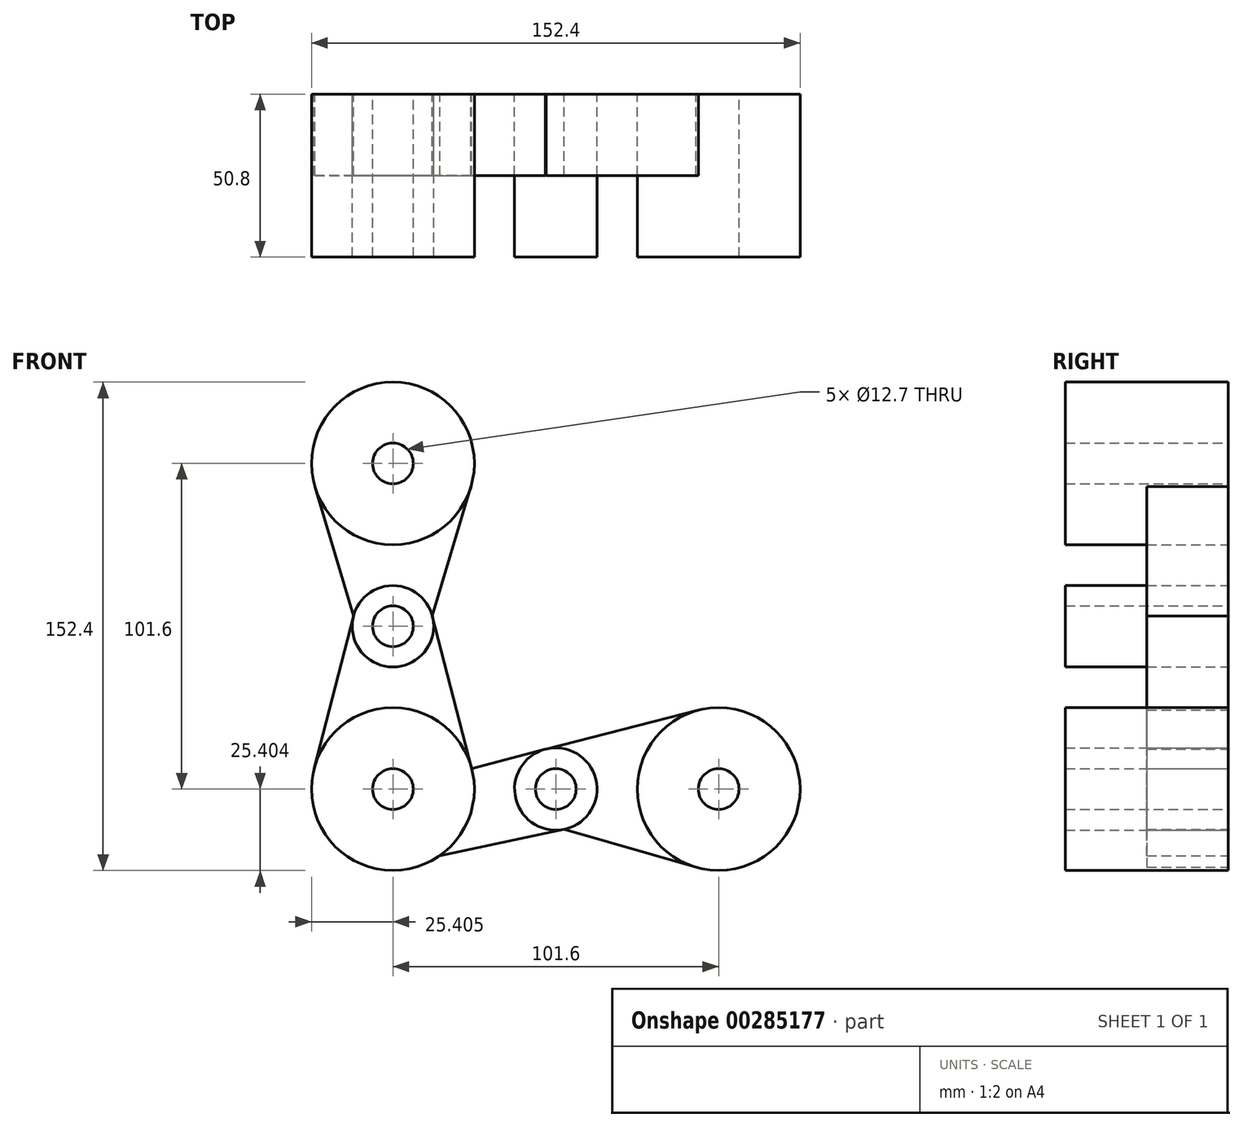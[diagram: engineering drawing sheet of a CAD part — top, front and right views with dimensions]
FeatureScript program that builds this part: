
annotation { "Feature Type Name" : "Feature", "Feature Type Description" : "" }
export const myFeature = defineFeature(function(context is Context, id is Id, definition is map)
    precondition{}
    {
        {
            var Q0;
            Q0=qCreatedBy(makeId("Front.planeOp"),FACE);
            var sketch = newSketch(context, id + "F0", { "sketchPlane" : qUnion([Q0])});
            skLineSegment(sketch, "E0", {"start": v(-81.49, -71.66) * mm, "end": v(-30.69, -71.66) * mm});
            skLineSegment(sketch, "E1", {"start": v(-30.69, -71.66) * mm, "end": v(20.11, -71.66) * mm});
            skLineSegment(sketch, "E2", {"start": v(-81.49, -71.66) * mm, "end": v(-81.49, -20.86) * mm});
            skLineSegment(sketch, "E3", {"start": v(-81.49, -20.86) * mm, "end": v(-81.49, 29.94) * mm});
            skCircle(sketch, "E4", {"center": v(20.11, -71.66) * mm, "radius": 25.4 * mm});
            skCircle(sketch, "E5", {"center": v(-81.49, -71.66) * mm, "radius": 25.4 * mm});
            skCircle(sketch, "E6", {"center": v(-81.49, 29.94) * mm, "radius": 25.4 * mm});
            skCircle(sketch, "E7", {"center": v(-81.49, -20.86) * mm, "radius": 12.7 * mm});
            skCircle(sketch, "E8", {"center": v(-30.69, -71.66) * mm, "radius": 12.85 * mm});
            skLineSegment(sketch, "E9", {"start": v(-57.15, 22.68) * mm, "end": v(-69.19, -17.68) * mm});
            skLineSegment(sketch, "E10", {"start": v(-69.19, -17.68) * mm, "end": v(-56.9, -65.3) * mm});
            skLineSegment(sketch, "E11", {"start": v(-56.9, -65.3) * mm, "end": v(-33.97, -59.24) * mm});
            skLineSegment(sketch, "E12", {"start": v(-33.97, -59.24) * mm, "end": v(13.84, -47.04) * mm});
            skLineSegment(sketch, "E13", {"start": v(-105.82, 22.68) * mm, "end": v(-93.78, -17.68) * mm});
            skLineSegment(sketch, "E14", {"start": v(-93.78, -17.68) * mm, "end": v(-106.08, -65.3) * mm});
            skLineSegment(sketch, "E15", {"start": v(-66.84, -92.4) * mm, "end": v(-28.03, -84.23) * mm});
            skLineSegment(sketch, "E16", {"start": v(-28.03, -84.23) * mm, "end": v(13.09, -96.06) * mm});
            skSolve(sketch);
        }
        {
            var Q0;
            {var subQ0=sQuery(id+"F0.wireOp",EDGE,"E6");var subQ1=makeQuery(id+"F0.imprint","INTERSECT",VERTEX,{"derivedFrom":[subQ0,sQuery(id+"F0.wireOp",EDGE,"E13")]});Q0=makeQuery(id+"F0.imprint","IMPRINT",FACE,{"disambiguationData":[TD([[makeQuery(id+"F0.imprint","IMPRINT",EDGE,{"disambiguationData":[TD([[subQ1,-1.0]])],"derivedFrom":subQ0}),1.0]])]});}
            var Q1;
            {var subQ3=sQuery(id+"F0.wireOp",EDGE,"E2");var subQ4=sQuery(id+"F0.wireOp",EDGE,"E0");var subQ5=makeQuery(id+"F0.imprint","INTERSECT",VERTEX,{"derivedFrom":[subQ4,subQ3]});Q1=makeQuery(id+"F0.imprint","IMPRINT",FACE,{"disambiguationData":[TD([[makeQuery(id+"F0.imprint","IMPRINT",EDGE,{"disambiguationData":[TD([[subQ5,-1.0]])],"derivedFrom":subQ4}),-1.0]])]});}
            var Q2;
            {var subQ0=sQuery(id+"F0.wireOp",EDGE,"E4");var subQ1=makeQuery(id+"F0.imprint","INTERSECT",VERTEX,{"derivedFrom":[subQ0,sQuery(id+"F0.wireOp",EDGE,"E12")]});Q2=makeQuery(id+"F0.imprint","IMPRINT",FACE,{"disambiguationData":[TD([[makeQuery(id+"F0.imprint","IMPRINT",EDGE,{"disambiguationData":[TD([[subQ1,-1.0]])],"derivedFrom":subQ0}),1.0]])]});}
            var Q3;
            {var subQ0=sQuery(id+"F0.wireOp",EDGE,"E3");var subQ1=sQuery(id+"F0.wireOp",EDGE,"E2");var subQ2=makeQuery(id+"F0.imprint","INTERSECT",VERTEX,{"derivedFrom":[subQ1,subQ0]});Q3=makeQuery(id+"F0.imprint","IMPRINT",FACE,{"disambiguationData":[TD([[makeQuery(id+"F0.imprint","IMPRINT",EDGE,{"disambiguationData":[TD([[subQ2,1.0]])],"derivedFrom":subQ1}),1.0]])]});}
            var Q4;
            {var subQ0=sQuery(id+"F0.wireOp",EDGE,"E3");var subQ1=sQuery(id+"F0.wireOp",EDGE,"E2");var subQ2=makeQuery(id+"F0.imprint","INTERSECT",VERTEX,{"derivedFrom":[subQ1,subQ0]});Q4=makeQuery(id+"F0.imprint","IMPRINT",FACE,{"disambiguationData":[TD([[makeQuery(id+"F0.imprint","IMPRINT",EDGE,{"disambiguationData":[TD([[subQ2,1.0]])],"derivedFrom":subQ1}),-1.0]])]});}
            var Q5;
            {var subQ0=sQuery(id+"F0.wireOp",EDGE,"E2");var subQ1=sQuery(id+"F0.wireOp",EDGE,"E0");var subQ2=makeQuery(id+"F0.imprint","INTERSECT",VERTEX,{"derivedFrom":[subQ1,subQ0]});Q5=makeQuery(id+"F0.imprint","IMPRINT",FACE,{"disambiguationData":[TD([[makeQuery(id+"F0.imprint","IMPRINT",EDGE,{"disambiguationData":[TD([[subQ2,-1.0]])],"derivedFrom":subQ1}),1.0]])]});}
            var Q6;
            {var subQ3=sQuery(id+"F0.wireOp",EDGE,"E1");var subQ5=sQuery(id+"F0.wireOp",EDGE,"E0");var subQ6=makeQuery(id+"F0.imprint","INTERSECT",VERTEX,{"derivedFrom":[subQ5,subQ3]});Q6=makeQuery(id+"F0.imprint","IMPRINT",FACE,{"disambiguationData":[TD([[makeQuery(id+"F0.imprint","IMPRINT",EDGE,{"disambiguationData":[TD([[subQ6,1.0]])],"derivedFrom":subQ5}),1.0]])]});}
            var Q7;
            {var subQ0=sQuery(id+"F0.wireOp",EDGE,"E1");var subQ1=sQuery(id+"F0.wireOp",EDGE,"E0");var subQ2=makeQuery(id+"F0.imprint","INTERSECT",VERTEX,{"derivedFrom":[subQ1,subQ0]});Q7=makeQuery(id+"F0.imprint","IMPRINT",FACE,{"disambiguationData":[TD([[makeQuery(id+"F0.imprint","IMPRINT",EDGE,{"disambiguationData":[TD([[subQ2,1.0]])],"derivedFrom":subQ1}),-1.0]])]});}
            extrude(context, id + "F1", {"entities" : qUnion([Q0, Q1, Q2, Q3, Q4, Q5, Q6, Q7]), "depth" : 50.8 * mm});
        }
        {
            var Q0;
            {var subQ5=sQuery(id+"F0.wireOp",EDGE,"E13");Q0=makeQuery(id+"F0.imprint","IMPRINT",FACE,{"disambiguationData":[TD([[makeQuery(id+"F0.imprint","IMPRINT",EDGE,{"derivedFrom":subQ5}),1.0]])]});}
            var Q1;
            {var subQ5=sQuery(id+"F0.wireOp",EDGE,"E9");Q1=makeQuery(id+"F0.imprint","IMPRINT",FACE,{"disambiguationData":[TD([[makeQuery(id+"F0.imprint","IMPRINT",EDGE,{"derivedFrom":subQ5}),-1.0]])]});}
            var Q2;
            {var subQ5=sQuery(id+"F0.wireOp",EDGE,"E14");Q2=makeQuery(id+"F0.imprint","IMPRINT",FACE,{"disambiguationData":[TD([[makeQuery(id+"F0.imprint","IMPRINT",EDGE,{"derivedFrom":subQ5}),1.0]])]});}
            var Q3;
            {var subQ5=sQuery(id+"F0.wireOp",EDGE,"E10");Q3=makeQuery(id+"F0.imprint","IMPRINT",FACE,{"disambiguationData":[TD([[makeQuery(id+"F0.imprint","IMPRINT",EDGE,{"derivedFrom":subQ5}),-1.0]])]});}
            var Q4;
            {var subQ5=sQuery(id+"F0.wireOp",EDGE,"E11");Q4=makeQuery(id+"F0.imprint","IMPRINT",FACE,{"disambiguationData":[TD([[makeQuery(id+"F0.imprint","IMPRINT",EDGE,{"derivedFrom":subQ5}),-1.0]])]});}
            var Q5;
            {var subQ5=sQuery(id+"F0.wireOp",EDGE,"E15");Q5=makeQuery(id+"F0.imprint","IMPRINT",FACE,{"disambiguationData":[TD([[makeQuery(id+"F0.imprint","IMPRINT",EDGE,{"derivedFrom":subQ5}),1.0]])]});}
            var Q6;
            {var subQ0=sQuery(id+"F0.wireOp",EDGE,"E4");var subQ1=sQuery(id+"F0.wireOp",EDGE,"E1");var subQ2=makeQuery(id+"F0.imprint","INTERSECT",VERTEX,{"derivedFrom":[subQ1,subQ0]});Q6=makeQuery(id+"F0.imprint","IMPRINT",FACE,{"disambiguationData":[TD([[makeQuery(id+"F0.imprint","IMPRINT",EDGE,{"disambiguationData":[TD([[subQ2,1.0]])],"derivedFrom":subQ1}),1.0]])]});}
            var Q7;
            {var subQ5=sQuery(id+"F0.wireOp",EDGE,"E16");Q7=makeQuery(id+"F0.imprint","IMPRINT",FACE,{"disambiguationData":[TD([[makeQuery(id+"F0.imprint","IMPRINT",EDGE,{"derivedFrom":subQ5}),1.0]])]});}
            extrude(context, id + "F2", {"entities" : qUnion([Q0, Q1, Q2, Q3, Q4, Q5, Q6, Q7]), "depth" : 25.4 * mm});
        }
        {
            var Q0;
            Q0=sQuery(id+"F0.wireOp",VERTEX,"E3.end");
            var Q1;
            Q1=sQuery(id+"F0.wireOp",VERTEX,"E7.center");
            var Q2;
            Q2=sQuery(id+"F0.wireOp",VERTEX,"E5.center");
            var Q3;
            Q3=sQuery(id+"F0.wireOp",VERTEX,"E8.center");
            var Q4;
            Q4=sQuery(id+"F0.wireOp",VERTEX,"E4.center");
            var Q5;
            Q5=makeQuery(id+"F1.opExtrude","SWEPT_BODY",BODY,{"disambiguationData":[OSD([sQuery(id+"F0.wireOp",EDGE,"E6")])]});
            var Q6;
            Q6=makeQuery(id+"F1.opExtrude","SWEPT_BODY",BODY,{"disambiguationData":[OSD([sQuery(id+"F0.wireOp",EDGE,"E7")])]});
            var Q7;
            Q7=makeQuery(id+"F1.opExtrude","SWEPT_BODY",BODY,{"disambiguationData":[OSD([sQuery(id+"F0.wireOp",EDGE,"E5")])]});
            var Q8;
            Q8=makeQuery(id+"F1.opExtrude","SWEPT_BODY",BODY,{"disambiguationData":[OSD([sQuery(id+"F0.wireOp",EDGE,"E8"),sQuery(id+"F0.wireOp",EDGE,"E12")])]});
            var Q9;
            Q9=makeQuery(id+"F1.opExtrude","SWEPT_BODY",BODY,{"disambiguationData":[OSD([sQuery(id+"F0.wireOp",EDGE,"E4")])]});
            hole(context, id + "F3", {"style" : HoleStyle.SIMPLE, "endStyle" : HoleEndStyle.THROUGH, "oppositeDirection" : true, "holeDiameter" : 12.7 * mm, "tappedDepth" : 12.7 * mm, "tapClearance" : 3, "locations" : qUnion([Q0, Q1, Q2, Q3, Q4]), "scope" : qUnion([Q5, Q6, Q7, Q8, Q9])});
        }
    });
